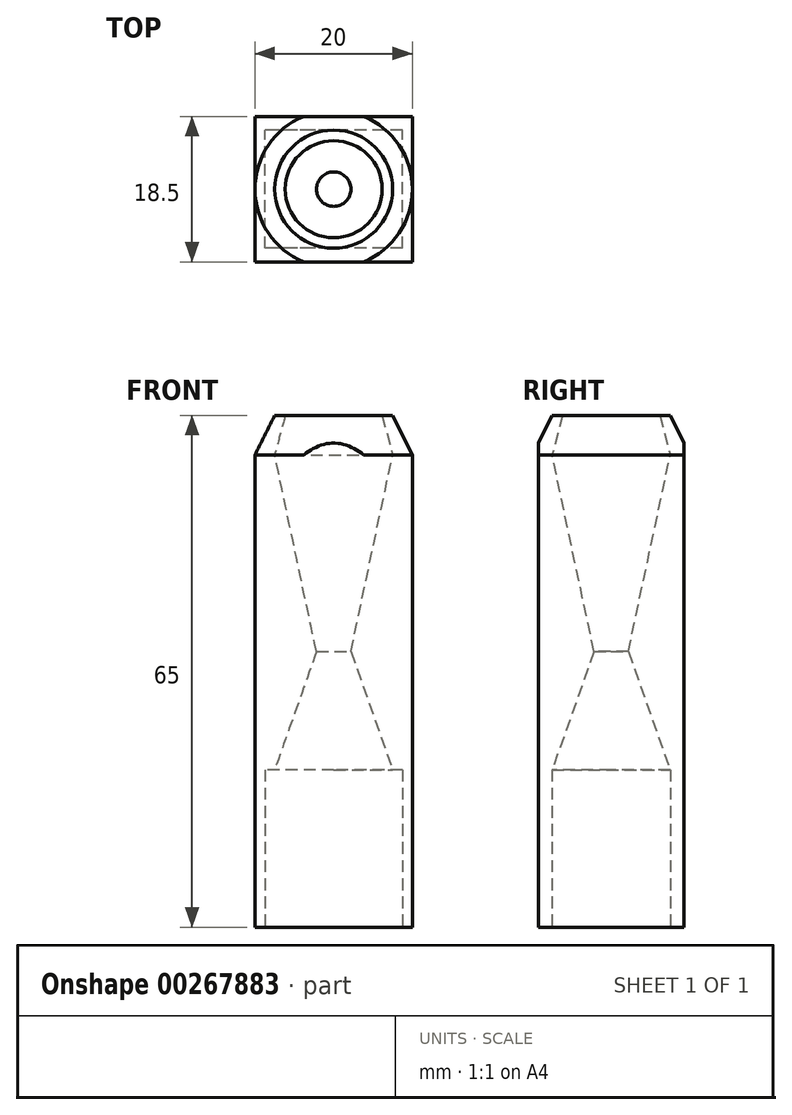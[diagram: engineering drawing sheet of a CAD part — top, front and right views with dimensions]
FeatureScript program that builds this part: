
annotation { "Feature Type Name" : "Feature", "Feature Type Description" : "" }
export const myFeature = defineFeature(function(context is Context, id is Id, definition is map)
    precondition{}
    {
        {
            var Q0;
            Q0=qCreatedBy(makeId("Front.planeOp"),FACE);
            var sketch = newSketch(context, id + "F0", { "sketchPlane" : qUnion([Q0])});
            skLineSegment(sketch, "E0", {"start": v(8.74, 7.02) * mm, "end": v(23.74, 7.02) * mm});
            skLineSegment(sketch, "E1", {"start": v(8.74, 7.02) * mm, "end": v(8.74, 67.02) * mm});
            skLineSegment(sketch, "E2", {"start": v(8.74, 67.02) * mm, "end": v(23.74, 67.02) * mm});
            skLineSegment(sketch, "E3", {"start": v(23.74, 67.02) * mm, "end": v(23.74, 7.02) * mm});
            skLineSegment(sketch, "E4", {"start": v(8.74, 7.02) * mm, "end": v(6.24, 7.02) * mm});
            skLineSegment(sketch, "E5", {"start": v(6.24, 7.02) * mm, "end": v(6.24, 67.02) * mm});
            skLineSegment(sketch, "E6", {"start": v(6.24, 67.02) * mm, "end": v(8.74, 67.02) * mm});
            skLineSegment(sketch, "E7", {"start": v(23.74, 67.02) * mm, "end": v(26.24, 67.02) * mm});
            skLineSegment(sketch, "E8", {"start": v(26.24, 67.02) * mm, "end": v(26.24, 7.02) * mm});
            skLineSegment(sketch, "E9", {"start": v(26.24, 7.02) * mm, "end": v(23.74, 7.02) * mm});
            skLineSegment(sketch, "E10", {"start": v(16.24, 7.02) * mm, "end": v(16.24, 72.02) * mm, "construction": true});
            skLineSegment(sketch, "E11", {"start": v(6.24, 67.02) * mm, "end": v(8.74, 72.02) * mm});
            skLineSegment(sketch, "E12", {"start": v(8.74, 72.02) * mm, "end": v(8.74, 67.02) * mm});
            skLineSegment(sketch, "E13", {"start": v(26.24, 67.02) * mm, "end": v(23.74, 72.02) * mm});
            skLineSegment(sketch, "E14", {"start": v(23.74, 72.02) * mm, "end": v(23.74, 67.02) * mm});
            skLineSegment(sketch, "E15", {"start": v(8.74, 72.02) * mm, "end": v(23.74, 72.02) * mm, "construction": true});
            skLineSegment(sketch, "E16", {"start": v(8.74, 67.02) * mm, "end": v(14.05, 42.02) * mm});
            skLineSegment(sketch, "E17", {"start": v(23.74, 67.02) * mm, "end": v(18.43, 42.02) * mm});
            skLineSegment(sketch, "E18", {"start": v(18.43, 42.02) * mm, "end": v(14.05, 42.02) * mm});
            skLineSegment(sketch, "E19", {"start": v(16.24, 7.02) * mm, "end": v(16.24, 42.02) * mm});
            skLineSegment(sketch, "E20", {"start": v(8.74, 27.02) * mm, "end": v(23.74, 27.02) * mm, "construction": true});
            skLineSegment(sketch, "E21", {"start": v(14.05, 42.02) * mm, "end": v(8.74, 27.02) * mm});
            skLineSegment(sketch, "E22", {"start": v(18.43, 42.02) * mm, "end": v(23.74, 27.02) * mm});
            skLineSegment(sketch, "E23", {"start": v(8.74, 27.02) * mm, "end": v(23.74, 27.02) * mm});
            skLineSegment(sketch, "E24", {"start": v(23.74, 67.02) * mm, "end": v(22.4, 72.02) * mm});
            skLineSegment(sketch, "E25", {"start": v(22.4, 72.02) * mm, "end": v(23.74, 72.02) * mm});
            skLineSegment(sketch, "E26", {"start": v(8.74, 67.02) * mm, "end": v(10.08, 72.02) * mm});
            skLineSegment(sketch, "E27", {"start": v(10.08, 72.02) * mm, "end": v(8.74, 72.02) * mm});
            skSolve(sketch);
        }
        {
            var Q0;
            {var subQ0=sQuery(id+"F0.wireOp",EDGE,"E17");Q0=makeQuery(id+"F0.imprint","IMPRINT",FACE,{"disambiguationData":[TD([[makeQuery(id+"F0.imprint","IMPRINT",EDGE,{"derivedFrom":subQ0}),1.0]])]});}
            var Q1;
            Q1=makeQuery(id+"F0.imprint","IMPRINT",FACE,{"disambiguationData":[TD([[makeQuery(id+"F0.imprint","IMPRINT",EDGE,{"derivedFrom":sQuery(id+"F0.wireOp",EDGE,"E14")}),-1.0]])]});
            var Q2;
            Q2=makeQuery(id+"F0.imprint","IMPRINT",FACE,{"disambiguationData":[TD([[makeQuery(id+"F0.imprint","IMPRINT",EDGE,{"derivedFrom":sQuery(id+"F0.wireOp",EDGE,"E7")}),1.0]])]});
            var Q3;
            Q3=sQuery(id+"F0.wireOp",EDGE,"E10");
            revolve(context, id + "F1", {"entities" : qUnion([Q0, Q1, Q2]), "axis" : qUnion([Q3]), "revolveType" : RevolveType.FULL});
        }
        {
            var Q0;
            {var subQ3=sQuery(id+"F0.wireOp",EDGE,"E4");Q0=makeQuery(id+"F0.imprint","IMPRINT",FACE,{"disambiguationData":[TD([[makeQuery(id+"F0.imprint","IMPRINT",EDGE,{"derivedFrom":subQ3}),-1.0]])]});}
            var Q1;
            {var subQ3=sQuery(id+"F0.wireOp",EDGE,"E7");Q1=makeQuery(id+"F0.imprint","IMPRINT",FACE,{"disambiguationData":[TD([[makeQuery(id+"F0.imprint","IMPRINT",EDGE,{"derivedFrom":subQ3}),-1.0]])]});}
            var Q2;
            {var subQ1=sQuery(id+"F0.wireOp",EDGE,"E0");var subQ3=sQuery(id+"F0.wireOp",EDGE,"E19");var subQ4=makeQuery(id+"F0.imprint","INTERSECT",VERTEX,{"derivedFrom":[subQ1,subQ3]});Q2=makeQuery(id+"F0.imprint","IMPRINT",FACE,{"disambiguationData":[TD([[makeQuery(id+"F0.imprint","IMPRINT",EDGE,{"disambiguationData":[TD([[subQ4,-1.0]])],"derivedFrom":subQ3}),1.0]])]});}
            var Q3;
            {var subQ1=sQuery(id+"F0.wireOp",EDGE,"E0");var subQ3=sQuery(id+"F0.wireOp",EDGE,"E19");var subQ4=makeQuery(id+"F0.imprint","INTERSECT",VERTEX,{"derivedFrom":[subQ1,subQ3]});Q3=makeQuery(id+"F0.imprint","IMPRINT",FACE,{"disambiguationData":[TD([[makeQuery(id+"F0.imprint","IMPRINT",EDGE,{"disambiguationData":[TD([[subQ4,-1.0]])],"derivedFrom":subQ3}),-1.0]])]});}
            extrude(context, id + "F2", {"entities" : qUnion([Q0, Q1, Q2, Q3]), "endBound" : BoundingType.SYMMETRIC, "depth" : 18.5 * mm});
        }
        {
            var Q0;
            Q0=makeQuery(id+"F2.opExtrude","SWEPT_FACE",FACE,{"disambiguationData":[OSD([sQuery(id+"F0.wireOp",EDGE,"E23")])]});
            var sketch = newSketch(context, id + "F3", { "sketchPlane" : qUnion([Q0])});
            skLineSegment(sketch, "E28.0.0", {"start": v(23.74, 9.25) * mm, "end": v(8.74, 9.25) * mm});
            skLineSegment(sketch, "E28.0.1", {"start": v(8.74, 9.25) * mm, "end": v(8.74, -9.25) * mm});
            skLineSegment(sketch, "E28.0.2", {"start": v(8.74, -9.25) * mm, "end": v(23.74, -9.25) * mm});
            skLineSegment(sketch, "E28.0.3", {"start": v(23.74, -9.25) * mm, "end": v(23.74, 9.25) * mm});
            skCircle(sketch, "E29.0", {"center": v(16.24, 0) * mm, "radius": 7.5 * mm});
            skSolve(sketch);
        }
        {
            var Q0;
            {var subQ0=sQuery(id+"F3.wireOp",EDGE,"E28.0.3");var subQ1=sQuery(id+"F3.wireOp",EDGE,"E28.0.2");var subQ2=makeQuery(id+"F3.imprint","INTERSECT",VERTEX,{"derivedFrom":[subQ1,subQ0]});Q0=makeQuery(id+"F3.imprint","IMPRINT",FACE,{"disambiguationData":[TD([[makeQuery(id+"F3.imprint","IMPRINT",EDGE,{"disambiguationData":[TD([[subQ2,1.0]])],"derivedFrom":subQ1}),1.0]])]});}
            var Q1;
            {var subQ0=sQuery(id+"F3.wireOp",EDGE,"E28.0.2");var subQ1=sQuery(id+"F3.wireOp",EDGE,"E28.0.1");var subQ2=makeQuery(id+"F3.imprint","INTERSECT",VERTEX,{"derivedFrom":[subQ1,subQ0]});Q1=makeQuery(id+"F3.imprint","IMPRINT",FACE,{"disambiguationData":[TD([[makeQuery(id+"F3.imprint","IMPRINT",EDGE,{"disambiguationData":[TD([[subQ2,-1.0]])],"derivedFrom":subQ1}),-1.0]])]});}
            var Q2;
            {var subQ0=sQuery(id+"F3.wireOp",EDGE,"E28.0.1");var subQ1=sQuery(id+"F3.wireOp",EDGE,"E28.0.0");var subQ2=makeQuery(id+"F3.imprint","INTERSECT",VERTEX,{"derivedFrom":[subQ1,subQ0]});Q2=makeQuery(id+"F3.imprint","IMPRINT",FACE,{"disambiguationData":[TD([[makeQuery(id+"F3.imprint","IMPRINT",EDGE,{"disambiguationData":[TD([[subQ2,-1.0]])],"derivedFrom":subQ1}),-1.0]])]});}
            var Q3;
            {var subQ0=sQuery(id+"F3.wireOp",EDGE,"E28.0.3");var subQ1=sQuery(id+"F3.wireOp",EDGE,"E28.0.0");var subQ2=makeQuery(id+"F3.imprint","INTERSECT",VERTEX,{"derivedFrom":[subQ1,subQ0]});Q3=makeQuery(id+"F3.imprint","IMPRINT",FACE,{"disambiguationData":[TD([[makeQuery(id+"F3.imprint","IMPRINT",EDGE,{"disambiguationData":[TD([[subQ2,1.0]])],"derivedFrom":subQ1}),-1.0]])]});}
            var Q4;
            Q4=makeQuery(id+"F1.opRevolve","SWEPT_FACE",FACE,{"disambiguationData":[OSD([sQuery(id+"F0.wireOp",EDGE,"E7")])]});
            extrude(context, id + "F4", {"entities" : qUnion([Q0, Q1, Q2, Q3]), "endBound" : BoundingType.UP_TO_SURFACE, "endBoundEntityFace" : qUnion([Q4]), "depth" : 25 * mm});
        }
        {
            var Q0;
            Q0=makeQuery(id+"F2.opExtrude","SWEPT_FACE",FACE,{"disambiguationData":[OSD([sQuery(id+"F0.wireOp",EDGE,"E0"),sQuery(id+"F0.wireOp",EDGE,"E4"),sQuery(id+"F0.wireOp",EDGE,"E9")])]});
            var sketch = newSketch(context, id + "F5", { "sketchPlane" : qUnion([Q0])});
            skLineSegment(sketch, "E30.0", {"start": v(26.24, 9.25) * mm, "end": v(6.24, 9.25) * mm});
            skLineSegment(sketch, "E31.0", {"start": v(26.24, 9.25) * mm, "end": v(26.24, -9.25) * mm});
            skSolve(sketch);
        }
        {
            var Q0;
            Q0=makeQuery(id+"F1.opRevolve","SWEPT_FACE",FACE,{"disambiguationData":[OSD([sQuery(id+"F0.wireOp",EDGE,"E7")])]});
            var sketch = newSketch(context, id + "F6", { "sketchPlane" : qUnion([Q0])});
            skCircle(sketch, "E32.0.0", {"center": v(16.24, 0) * mm, "radius": 10 * mm});
            skLineSegment(sketch, "E33.0", {"start": v(8.74, -9.25) * mm, "end": v(8.74, -9.25) * mm});
            skLineSegment(sketch, "E34.0", {"start": v(23.74, -9.25) * mm, "end": v(8.74, -9.25) * mm});
            skLineSegment(sketch, "E35.0", {"start": v(8.74, 9.25) * mm, "end": v(8.74, 9.25) * mm});
            skLineSegment(sketch, "E36.0", {"start": v(23.74, 9.25) * mm, "end": v(8.74, 9.25) * mm});
            skSolve(sketch);
        }
        {
            var Q0;
            {var subQ0=sQuery(id+"F6.wireOp",EDGE,"E36.0");var subQ1=sQuery(id+"F6.wireOp",EDGE,"E32.0.0");var subQ2=makeQuery(id+"F6.imprint","INTERSECT",VERTEX,{"derivedFrom":[subQ1,subQ0]});Q0=makeQuery(id+"F6.imprint","IMPRINT",FACE,{"disambiguationData":[TD([[makeQuery(id+"F6.imprint","IMPRINT",EDGE,{"disambiguationData":[TD([[subQ2,-1.0]])],"derivedFrom":subQ1}),1.0]])]});}
            var Q1;
            {var subQ0=sQuery(id+"F6.wireOp",EDGE,"E34.0");var subQ1=sQuery(id+"F6.wireOp",EDGE,"E32.0.0");var subQ2=makeQuery(id+"F6.imprint","INTERSECT",VERTEX,{"derivedFrom":[subQ1,subQ0]});Q1=makeQuery(id+"F6.imprint","IMPRINT",FACE,{"disambiguationData":[TD([[makeQuery(id+"F6.imprint","IMPRINT",EDGE,{"disambiguationData":[TD([[subQ2,1.0]])],"derivedFrom":subQ1}),1.0]])]});}
            var Q2;
            Q2=makeQuery(id+"F1.opRevolve","SWEPT_FACE",FACE,{"disambiguationData":[OSD([sQuery(id+"F0.wireOp",EDGE,"E25")])]});
            extrude(context, id + "F7", {"entities" : qUnion([Q0, Q1]), "operationType" : NewBodyOperationType.REMOVE, "endBound" : BoundingType.UP_TO_SURFACE, "oppositeDirection" : true, "endBoundEntityFace" : qUnion([Q2]), "depth" : 25 * mm});
        }
        {
            var Q0;
            Q0=makeQuery(id+"F4.opExtrude","SWEPT_BODY",BODY,{"disambiguationData":[OSD([sQuery(id+"F3.wireOp",EDGE,"E28.0.1"),sQuery(id+"F3.wireOp",EDGE,"E28.0.2"),sQuery(id+"F3.wireOp",EDGE,"E29.0")])]});
            var Q1;
            Q1=makeQuery(id+"F1.opRevolve","SWEPT_BODY",BODY,{"disambiguationData":[OSD([sQuery(id+"F0.wireOp",EDGE,"E7"),sQuery(id+"F0.wireOp",EDGE,"E13"),sQuery(id+"F0.wireOp",EDGE,"E24"),sQuery(id+"F0.wireOp",EDGE,"E25")])]});
            var Q2;
            Q2=makeQuery(id+"F2.opExtrude","SWEPT_BODY",BODY,{"disambiguationData":[OSD([sQuery(id+"F0.wireOp",EDGE,"E0"),sQuery(id+"F0.wireOp",EDGE,"E1"),sQuery(id+"F0.wireOp",EDGE,"E3"),sQuery(id+"F0.wireOp",EDGE,"E4"),sQuery(id+"F0.wireOp",EDGE,"E5"),sQuery(id+"F0.wireOp",EDGE,"E6"),sQuery(id+"F0.wireOp",EDGE,"E7"),sQuery(id+"F0.wireOp",EDGE,"E8"),sQuery(id+"F0.wireOp",EDGE,"E9"),sQuery(id+"F0.wireOp",EDGE,"E23")])]});
            var Q3;
            Q3=makeQuery(id+"F4.opExtrude","SWEPT_BODY",BODY,{"disambiguationData":[OSD([sQuery(id+"F3.wireOp",EDGE,"E28.0.2"),sQuery(id+"F3.wireOp",EDGE,"E28.0.3"),sQuery(id+"F3.wireOp",EDGE,"E29.0")])]});
            var Q4;
            Q4=makeQuery(id+"F1.opRevolve","SWEPT_BODY",BODY,{"disambiguationData":[OSD([sQuery(id+"F0.wireOp",EDGE,"E3"),sQuery(id+"F0.wireOp",EDGE,"E17"),sQuery(id+"F0.wireOp",EDGE,"E22")])]});
            var Q5;
            Q5=makeQuery(id+"F4.opExtrude","SWEPT_BODY",BODY,{"disambiguationData":[OSD([sQuery(id+"F3.wireOp",EDGE,"E28.0.0"),sQuery(id+"F3.wireOp",EDGE,"E28.0.3"),sQuery(id+"F3.wireOp",EDGE,"E29.0")])]});
            var Q6;
            Q6=makeQuery(id+"F4.opExtrude","SWEPT_BODY",BODY,{"disambiguationData":[OSD([sQuery(id+"F3.wireOp",EDGE,"E28.0.0"),sQuery(id+"F3.wireOp",EDGE,"E28.0.1"),sQuery(id+"F3.wireOp",EDGE,"E29.0")])]});
            booleanBodies(context, id + "F8", {"operationType" : BooleanOperationType.UNION, "tools" : qUnion([Q0, Q1, Q2, Q3, Q4, Q5, Q6])});
        }
        {
            var Q0;
            Q0=makeQuery(id+"F5.imprint","IMPRINT",FACE,{"disambiguationData":[TD([[makeQuery(id+"F5.imprint","IMPRINT",EDGE,{"derivedFrom":sQuery(id+"F5.wireOp",EDGE,"E30.0")}),1.0]])]});
            var sketch = newSketch(context, id + "F9", { "sketchPlane" : qUnion([Q0])});
            skLineSegment(sketch, "E37.0", {"start": v(26.24, 9.25) * mm, "end": v(6.24, 9.25) * mm});
            skLineSegment(sketch, "E38.0", {"start": v(26.24, 9.25) * mm, "end": v(26.24, -9.25) * mm});
            skPoint(sketch, "E39.0", {"position": v(26.24, 0) * mm});
            skPoint(sketch, "E40.0", {"position": v(16.24, -9.25) * mm});
            skLineSegment(sketch, "E41.bottom", {"start": v(24.99, 7.5) * mm, "end": v(7.49, 7.5) * mm});
            skLineSegment(sketch, "E41.top", {"start": v(24.99, -7.5) * mm, "end": v(7.49, -7.5) * mm});
            skLineSegment(sketch, "E41.left", {"start": v(24.99, 7.5) * mm, "end": v(24.99, -7.5) * mm});
            skLineSegment(sketch, "E41.right", {"start": v(7.49, 7.5) * mm, "end": v(7.49, -7.5) * mm});
            skPoint(sketch, "E41.middle", {"position": v(16.24, 0) * mm});
            skSolve(sketch);
        }
        {
            var Q0;
            Q0=makeQuery(id+"F9.imprint","IMPRINT",FACE,{"disambiguationData":[TD([[makeQuery(id+"F9.imprint","IMPRINT",EDGE,{"derivedFrom":sQuery(id+"F9.wireOp",EDGE,"E41.bottom")}),1.0]])]});
            extrude(context, id + "F10", {"entities" : qUnion([Q0]), "operationType" : NewBodyOperationType.REMOVE, "oppositeDirection" : true, "depth" : 20 * mm});
        }
    });
